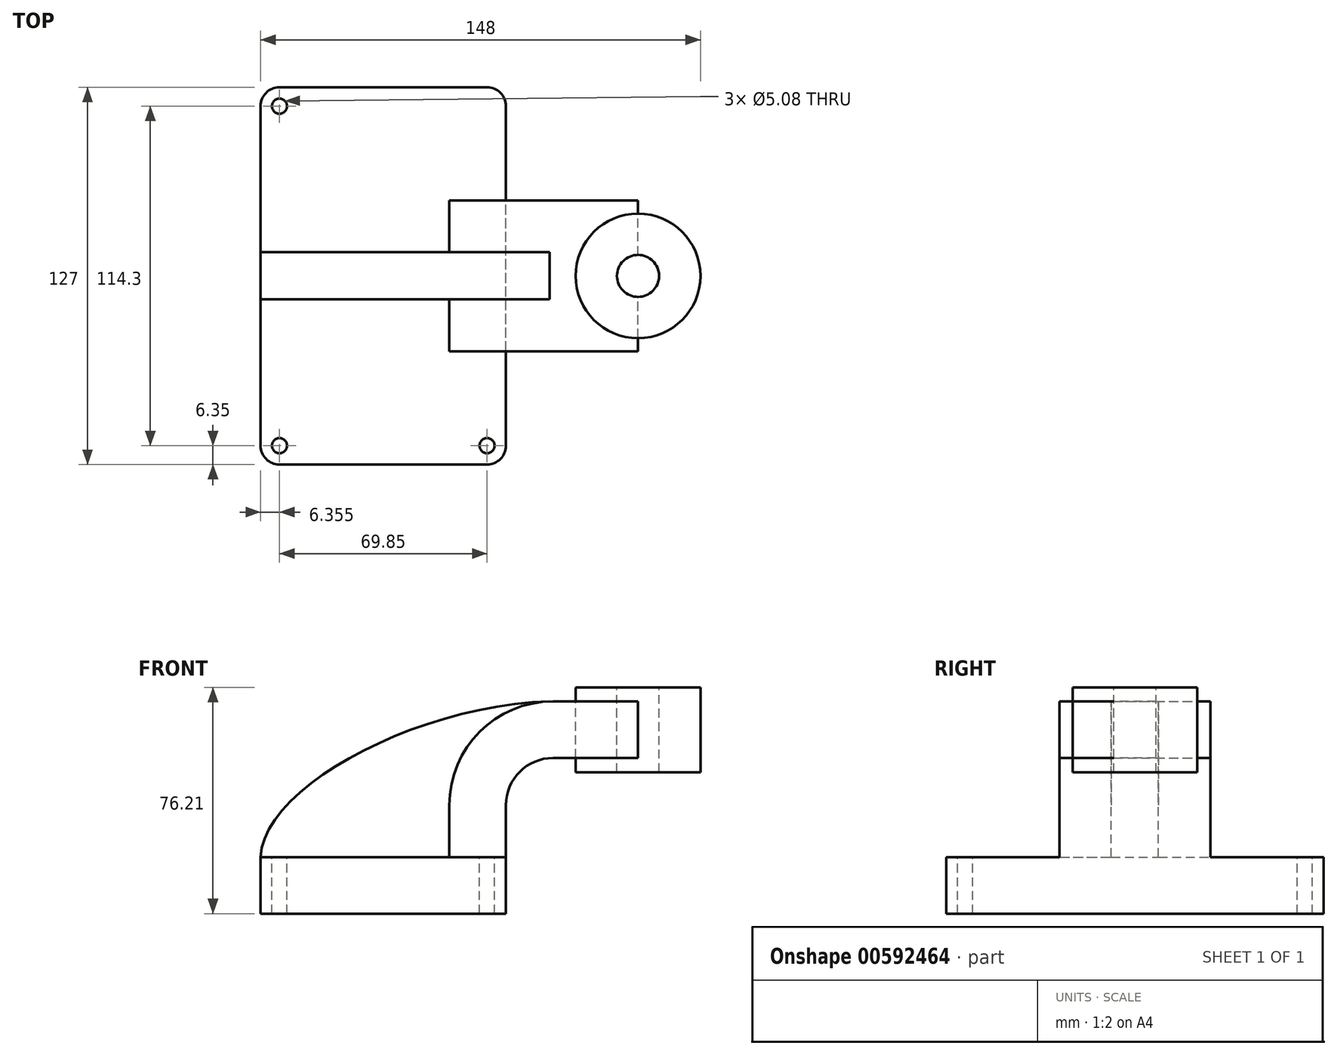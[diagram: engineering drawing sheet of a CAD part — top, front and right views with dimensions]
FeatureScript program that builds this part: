
annotation { "Feature Type Name" : "Feature", "Feature Type Description" : "" }
export const myFeature = defineFeature(function(context is Context, id is Id, definition is map)
    precondition{}
    {
        {
            var Q0;
            Q0=qCreatedBy(makeId("Front.planeOp"),FACE);
            var sketch = newSketch(context, id + "F0", { "sketchPlane" : qUnion([Q0])});
            skLineSegment(sketch, "E0.bottom", {"start": v(41.27, 9.53) * mm, "end": v(-41.28, 9.53) * mm});
            skLineSegment(sketch, "E0.top", {"start": v(41.28, -9.52) * mm, "end": v(-41.27, -9.52) * mm});
            skLineSegment(sketch, "E0.left", {"start": v(41.27, 9.53) * mm, "end": v(41.28, -9.52) * mm});
            skLineSegment(sketch, "E0.right", {"start": v(-41.28, 9.53) * mm, "end": v(-41.27, -9.52) * mm});
            skPoint(sketch, "E0.middle", {"position": v(0, 0) * mm});
            skLineSegment(sketch, "E1.bottom", {"start": v(55.92, 38.1) * mm, "end": v(106.72, 38.1) * mm});
            skLineSegment(sketch, "E1.top", {"start": v(55.92, 66.68) * mm, "end": v(106.72, 66.68) * mm});
            skLineSegment(sketch, "E1.left", {"start": v(55.92, 38.1) * mm, "end": v(55.92, 66.68) * mm});
            skLineSegment(sketch, "E1.right", {"start": v(106.72, 38.1) * mm, "end": v(106.72, 66.68) * mm});
            skPoint(sketch, "E1.middle", {"position": v(81.32, 52.39) * mm});
            skLineSegment(sketch, "E2", {"start": v(41.27, 9.53) * mm, "end": v(41.27, 27) * mm});
            skArc(sketch, "E3", {"start": v(41.27, 27) * mm, "mid": v(45.92, 38.23) * mm, "end": v(57.15, 42.88) * mm});
            skLineSegment(sketch, "E4", {"start": v(57.15, 42.88) * mm, "end": v(85.72, 42.88) * mm});
            skLineSegment(sketch, "E5.0", {"start": v(57.15, 61.93) * mm, "end": v(85.72, 61.93) * mm});
            skArc(sketch, "E5.1", {"start": v(22.22, 27) * mm, "mid": v(32.45, 51.7) * mm, "end": v(57.15, 61.93) * mm});
            skLineSegment(sketch, "E5.2", {"start": v(22.22, 9.53) * mm, "end": v(22.22, 27) * mm});
            skPoint(sketch, "E6.1.internal.snap0", {"position": v(71.44, 61.93) * mm});
            skFitSpline(sketch, "E6", {"points": [v(-41.28, 9.53) * mm, v(55.92, 61.93) * mm], "startDerivative": vector(2.57, 70.81) * mm, "endDerivative": vector(133.32, 3.82) * mm});
            skLineSegment(sketch, "E7", {"start": v(85.72, 61.93) * mm, "end": v(85.72, 42.88) * mm});
            skLineSegment(sketch, "E8", {"start": v(85.72, 66.68) * mm, "end": v(85.72, 38.1) * mm});
            skSolve(sketch);
        }
        {
            var Q0;
            Q0=makeQuery(id+"F0.imprint","IMPRINT",FACE,{"disambiguationData":[TD([[makeQuery(id+"F0.imprint","IMPRINT",EDGE,{"derivedFrom":sQuery(id+"F0.wireOp",EDGE,"E0.top")}),-1.0]])]});
            extrude(context, id + "F1", {"entities" : qUnion([Q0]), "endBound" : BoundingType.SYMMETRIC, "depth" : 127 * mm, "offsetDistance" : 25.4 * mm});
        }
        {
            var Q0;
            {var subQ0=sQuery(id+"F0.wireOp",EDGE,"E2");Q0=makeQuery(id+"F0.imprint","IMPRINT",FACE,{"disambiguationData":[TD([[makeQuery(id+"F0.imprint","IMPRINT",EDGE,{"derivedFrom":subQ0}),1.0]])]});}
            var Q1;
            {var subQ1=sQuery(id+"F0.wireOp",EDGE,"E4");Q1=makeQuery(id+"F0.imprint","IMPRINT",FACE,{"disambiguationData":[TD([[makeQuery(id+"F0.imprint","IMPRINT",EDGE,{"derivedFrom":subQ1}),1.0]])]});}
            extrude(context, id + "F2", {"entities" : qUnion([Q0, Q1]), "operationType" : NewBodyOperationType.ADD, "endBound" : BoundingType.SYMMETRIC, "depth" : 50.8 * mm, "offsetDistance" : 25.4 * mm});
        }
        {
            var Q0;
            {var subQ0=sQuery(id+"F0.wireOp",EDGE,"E5.2");Q0=makeQuery(id+"F0.imprint","IMPRINT",FACE,{"disambiguationData":[TD([[makeQuery(id+"F0.imprint","IMPRINT",EDGE,{"derivedFrom":subQ0}),1.0]])]});}
            extrude(context, id + "F3", {"entities" : qUnion([Q0]), "operationType" : NewBodyOperationType.ADD, "endBound" : BoundingType.SYMMETRIC, "depth" : 15.88 * mm, "offsetDistance" : 25.4 * mm});
        }
        {
            var Q0;
            Q0=makeQuery(id+"F1.opExtrude","CAP_EDGE",EDGE,{"disambiguationData":[OSD([sQuery(id+"F0.wireOp",EDGE,"E0.left")])],"isStart":false});
            var Q1;
            Q1=makeQuery(id+"F1.opExtrude","CAP_EDGE",EDGE,{"disambiguationData":[OSD([sQuery(id+"F0.wireOp",EDGE,"E0.right")])],"isStart":false});
            var Q2;
            Q2=makeQuery(id+"F1.opExtrude","CAP_EDGE",EDGE,{"disambiguationData":[OSD([sQuery(id+"F0.wireOp",EDGE,"E0.left")])],"isStart":true});
            var Q3;
            Q3=makeQuery(id+"F1.opExtrude","CAP_EDGE",EDGE,{"disambiguationData":[OSD([sQuery(id+"F0.wireOp",EDGE,"E0.right")])],"isStart":true});
            fillet(context, id + "F4", {"entities" : qUnion([Q0, Q1, Q2, Q3]), "radius" : 6.35 * mm, "tangentPropagation" : true, "allowEdgeOverflow" : false});
        }
        {
            var Q0;
            {var subQ4=sQuery(id+"F0.wireOp",EDGE,"E1.right");Q0=makeQuery(id+"F0.imprint","IMPRINT",FACE,{"disambiguationData":[TD([[makeQuery(id+"F0.imprint","IMPRINT",EDGE,{"derivedFrom":subQ4}),1.0]])]});}
            var Q1;
            Q1=sQuery(id+"F0.wireOp",EDGE,"E8");
            revolve(context, id + "F5", {"entities" : qUnion([Q0]), "axis" : qUnion([Q1]), "revolveType" : RevolveType.FULL});
        }
        {
            var Q0;
            Q0=makeQuery(id+"F5.opRevolve","SWEPT_FACE",FACE,{"disambiguationData":[OSD([sQuery(id+"F0.wireOp",EDGE,"E1.top")])]});
            var sketch = newSketch(context, id + "F6", { "sketchPlane" : qUnion([Q0])});
            skCircle(sketch, "E9", {"center": v(85.72, 0) * mm, "radius": 7.08 * mm});
            skSolve(sketch);
        }
        {
            var Q0;
            Q0=makeQuery(id+"F6.imprint","IMPRINT",FACE,{"disambiguationData":[TD([[makeQuery(id+"F6.imprint","IMPRINT",EDGE,{"derivedFrom":sQuery(id+"F6.wireOp",EDGE,"E9")}),1.0]])]});
            extrude(context, id + "F7", {"entities" : qUnion([Q0]), "operationType" : NewBodyOperationType.REMOVE, "oppositeDirection" : true, "depth" : 34.54 * mm, "offsetDistance" : 25.4 * mm});
        }
        {
            var Q0;
            {var subQ3=sQuery(id+"F0.wireOp",EDGE,"E0.bottom");var subQ4=sQuery(id+"F0.wireOp",EDGE,"E0.right");var subQ5=sQuery(id+"F0.wireOp",EDGE,"E0.left");Q0=makeQuery(id+"F3.boolean.opBoolean","SPLIT",FACE,{"disambiguationData":[TD([makeQuery(id+"F1.opExtrude","CAP_FACE",FACE,{"disambiguationData":[OSD([subQ3,sQuery(id+"F0.wireOp",EDGE,"E0.top"),subQ5,subQ4])],"isStart":false})])],"derivedFrom":makeQuery(id+"F1.opExtrude","SWEPT_FACE",FACE,{"disambiguationData":[OSD([subQ3])]})});}
            var sketch = newSketch(context, id + "F8", { "sketchPlane" : qUnion([Q0])});
            skCircle(sketch, "E10", {"center": v(-34.93, -57.15) * mm, "radius": 2.54 * mm});
            skCircle(sketch, "E11", {"center": v(34.92, -57.15) * mm, "radius": 2.54 * mm});
            skSolve(sketch);
        }
        {
            var Q0;
            Q0=makeQuery(id+"F8.imprint","IMPRINT",FACE,{"disambiguationData":[TD([[makeQuery(id+"F8.imprint","IMPRINT",EDGE,{"derivedFrom":sQuery(id+"F8.wireOp",EDGE,"E10")}),1.0]])]});
            extrude(context, id + "F9", {"entities" : qUnion([Q0]), "operationType" : NewBodyOperationType.REMOVE, "oppositeDirection" : true, "depth" : 25.4 * mm, "offsetDistance" : 25.4 * mm});
        }
        {
            var Q0;
            {var subQ3=sQuery(id+"F0.wireOp",EDGE,"E0.bottom");var subQ4=sQuery(id+"F0.wireOp",EDGE,"E0.right");var subQ5=sQuery(id+"F0.wireOp",EDGE,"E0.left");Q0=makeQuery(id+"F3.boolean.opBoolean","SPLIT",FACE,{"disambiguationData":[TD([makeQuery(id+"F1.opExtrude","CAP_FACE",FACE,{"disambiguationData":[OSD([subQ3,sQuery(id+"F0.wireOp",EDGE,"E0.top"),subQ5,subQ4])],"isStart":true})])],"derivedFrom":makeQuery(id+"F1.opExtrude","SWEPT_FACE",FACE,{"disambiguationData":[OSD([subQ3])]})});}
            var sketch = newSketch(context, id + "F10", { "sketchPlane" : qUnion([Q0])});
            skCircle(sketch, "E12", {"center": v(-34.93, 57.15) * mm, "radius": 2.54 * mm});
            skCircle(sketch, "E13", {"center": v(34.92, 57.15) * mm, "radius": 2.54 * mm});
            skSolve(sketch);
        }
        {
            var Q0;
            Q0=makeQuery(id+"F10.imprint","IMPRINT",FACE,{"disambiguationData":[TD([[makeQuery(id+"F10.imprint","IMPRINT",EDGE,{"derivedFrom":sQuery(id+"F10.wireOp",EDGE,"E12")}),1.0]])]});
            var Q1;
            Q1=sQuery(id+"F10.wireOp",EDGE,"E12");
            extrude(context, id + "F11", {"entities" : qUnion([Q0]), "operationType" : NewBodyOperationType.REMOVE, "surfaceEntities" : qUnion([Q1]), "oppositeDirection" : true, "depth" : 25.4 * mm, "offsetDistance" : 25.4 * mm});
        }
        {
            var Q0;
            Q0=makeQuery(id+"F8.imprint","IMPRINT",FACE,{"disambiguationData":[TD([[makeQuery(id+"F8.imprint","IMPRINT",EDGE,{"derivedFrom":sQuery(id+"F8.wireOp",EDGE,"E11")}),1.0]])]});
            extrude(context, id + "F12", {"entities" : qUnion([Q0]), "operationType" : NewBodyOperationType.REMOVE, "oppositeDirection" : true, "depth" : 25.4 * mm, "offsetDistance" : 25.4 * mm});
        }
    });
